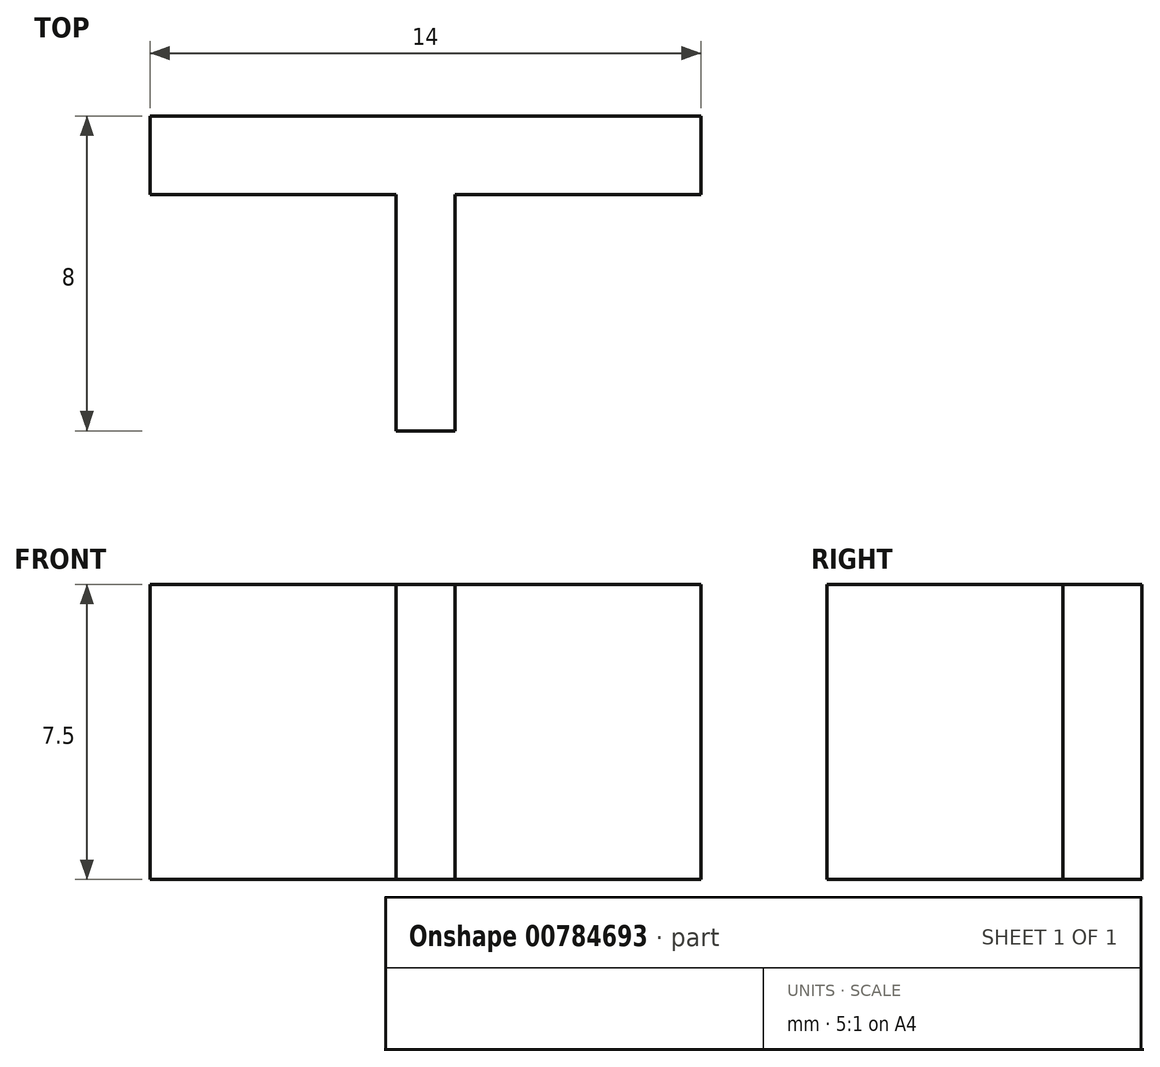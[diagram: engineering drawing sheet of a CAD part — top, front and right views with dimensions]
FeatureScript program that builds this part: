
annotation { "Feature Type Name" : "Feature", "Feature Type Description" : "" }
export const myFeature = defineFeature(function(context is Context, id is Id, definition is map)
    precondition{}
    {
        {
            var Q0;
            Q0=qCreatedBy(makeId("Top.planeOp"),FACE);
            var sketch = newSketch(context, id + "F0", { "sketchPlane" : qUnion([Q0])});
            skLineSegment(sketch, "E0", {"start": v(0, 0) * mm, "end": v(14, 0) * mm});
            skLineSegment(sketch, "E1", {"start": v(14, 0) * mm, "end": v(14, -2) * mm});
            skLineSegment(sketch, "E2", {"start": v(14, -2) * mm, "end": v(7.75, -2) * mm});
            skLineSegment(sketch, "E3", {"start": v(0, 0) * mm, "end": v(0, -2) * mm});
            skLineSegment(sketch, "E4", {"start": v(0, -2) * mm, "end": v(6.25, -2) * mm});
            skLineSegment(sketch, "E5", {"start": v(6.25, -2) * mm, "end": v(6.25, -8) * mm});
            skLineSegment(sketch, "E6", {"start": v(6.25, -8) * mm, "end": v(7.75, -8) * mm});
            skLineSegment(sketch, "E7", {"start": v(7.75, -8) * mm, "end": v(7.75, -2) * mm});
            skSolve(sketch);
        }
        {
            var Q0;
            Q0=makeQuery(id+"F0.imprint","IMPRINT",FACE,{"disambiguationData":[TD([[makeQuery(id+"F0.imprint","IMPRINT",EDGE,{"derivedFrom":sQuery(id+"F0.wireOp",EDGE,"E0")}),-1.0]])]});
            extrude(context, id + "F1", {"entities" : qUnion([Q0]), "depth" : 7.5 * mm, "offsetDistance" : 25 * mm});
        }
    });
